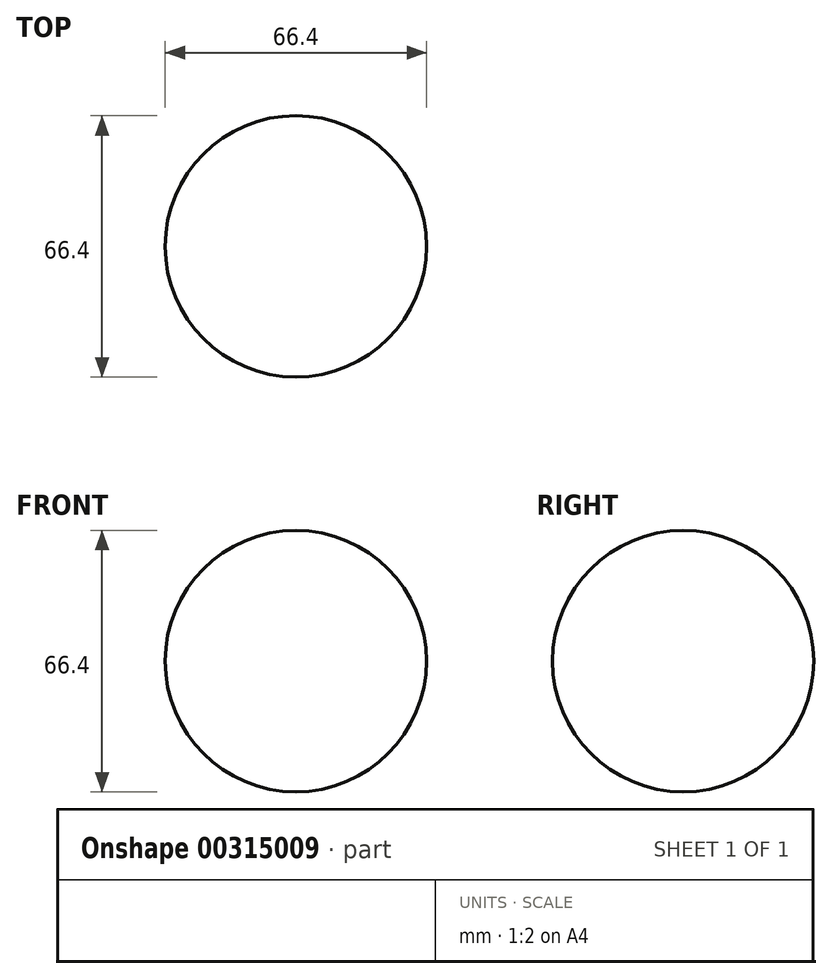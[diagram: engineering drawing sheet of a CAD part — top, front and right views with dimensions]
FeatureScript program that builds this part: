
annotation { "Feature Type Name" : "Feature", "Feature Type Description" : "" }
export const myFeature = defineFeature(function(context is Context, id is Id, definition is map)
    precondition{}
    {
        {
            var Q0;
            Q0=qCreatedBy(makeId("Front.planeOp"),FACE);
            var sketch = newSketch(context, id + "F0", { "sketchPlane" : qUnion([Q0])});
            skLineSegment(sketch, "E0", {"start": v(0, 32.8) * mm, "end": v(0, -33.2) * mm, "construction": true});
            skArc(sketch, "E1", {"start": v(0, -33.2) * mm, "mid": v(33.2, 0) * mm, "end": v(0, 33.2) * mm});
            skSolve(sketch);
        }
        {
            var Q0;
            Q0=sQuery(id+"F0.wireOp",EDGE,"E1");
            var Q1;
            Q1=sQuery(id+"F0.wireOp",EDGE,"E0");
            revolve(context, id + "F1", {"bodyType" : ToolBodyType.SURFACE, "surfaceEntities" : qUnion([Q0]), "axis" : qUnion([Q1]), "revolveType" : RevolveType.FULL});
        }
    });
